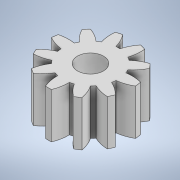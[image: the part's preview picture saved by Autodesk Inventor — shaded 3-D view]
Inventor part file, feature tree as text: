
AUTODESK INVENTOR PART (.ipt)
format: ipt  version: 2022 (Build 260153000, 153)  size: 165,888 bytes
history: native  units: mm
features: other x1, extrude x1, sketch x1
ambient origin geometry x8: Origin, YZ Plane, XZ Plane, XY Plane, X Axis, Y Axis, Z Axis, Center Point
bodies: Body1 (feature_tree)
feature tree (3):
  other  "Твердое тело1"
  extrude  "Выдавливание1"  Depth=7.0mm TaperAngle=0.0deg
  sketch  "Эскиз1"
